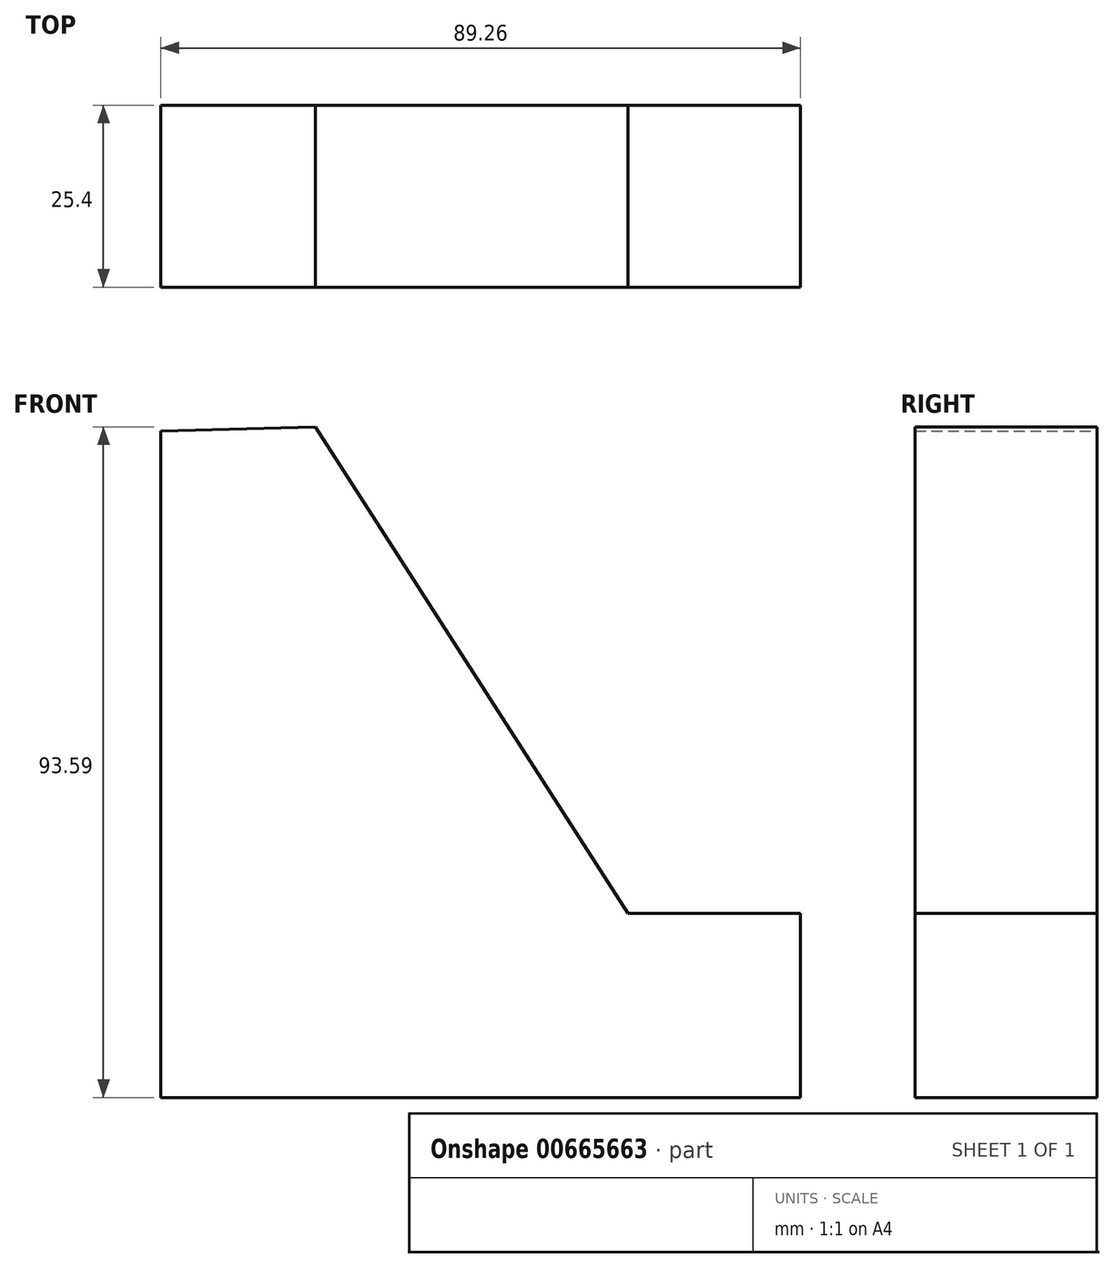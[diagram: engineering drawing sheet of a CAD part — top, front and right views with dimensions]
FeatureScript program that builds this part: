
annotation { "Feature Type Name" : "Feature", "Feature Type Description" : "" }
export const myFeature = defineFeature(function(context is Context, id is Id, definition is map)
    precondition{}
    {
        {
            var Q0;
            Q0=qCreatedBy(makeId("Front.planeOp"),FACE);
            var sketch = newSketch(context, id + "F0", { "sketchPlane" : qUnion([Q0])});
            skLineSegment(sketch, "E0", {"start": v(-31.98, 36.3) * mm, "end": v(-31.98, -56.67) * mm});
            skLineSegment(sketch, "E1", {"start": v(-31.98, -56.67) * mm, "end": v(57.28, -56.67) * mm});
            skLineSegment(sketch, "E2", {"start": v(57.28, -56.67) * mm, "end": v(57.28, -30.96) * mm});
            skLineSegment(sketch, "E3", {"start": v(57.28, -30.96) * mm, "end": v(33.22, -30.96) * mm});
            skLineSegment(sketch, "E4", {"start": v(33.22, -30.96) * mm, "end": v(-10.39, 36.92) * mm});
            skLineSegment(sketch, "E5", {"start": v(-10.39, 36.92) * mm, "end": v(-31.98, 36.3) * mm});
            skSolve(sketch);
        }
        {
            var Q0;
            Q0 = qSketchRegion(id + "F0", true);
            extrude(context, id + "F1", {"entities" : qUnion([Q0]), "depth" : 25.4 * mm, "offsetDistance" : 25.4 * mm});
        }
    });
